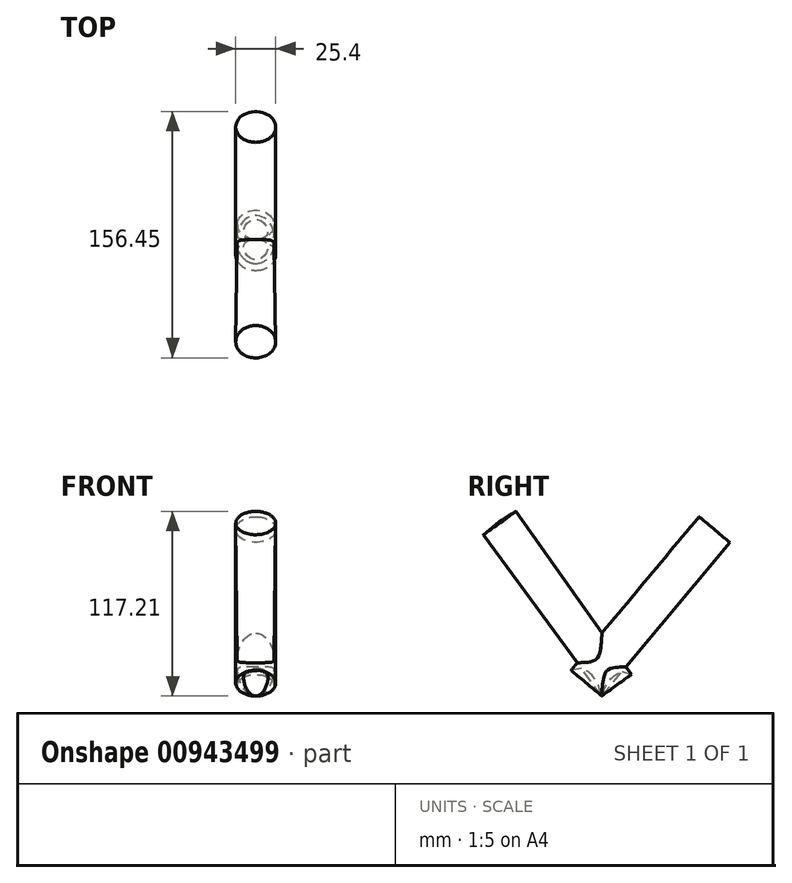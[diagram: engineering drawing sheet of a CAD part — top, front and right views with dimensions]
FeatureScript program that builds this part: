
annotation { "Feature Type Name" : "Feature", "Feature Type Description" : "" }
export const myFeature = defineFeature(function(context is Context, id is Id, definition is map)
    precondition{}
    {
        {
            var Q0;
            Q0=qCreatedBy(makeId("Right.planeOp"),FACE);
            var sketch = newSketch(context, id + "F0", { "sketchPlane" : qUnion([Q0])});
            skLineSegment(sketch, "E0", {"start": v(-105.27, 49.35) * mm, "end": v(-30.13, -53.04) * mm});
            skLineSegment(sketch, "E1", {"start": v(-30.13, -53.04) * mm, "end": v(51.18, 44.53) * mm});
            skLineSegment(sketch, "E2", {"start": v(51.18, 44.53) * mm, "end": v(41.42, 52.66) * mm});
            skLineSegment(sketch, "E3", {"start": v(41.42, 52.66) * mm, "end": v(-30.13, -33.2) * mm});
            skLineSegment(sketch, "E4", {"start": v(-30.13, -33.2) * mm, "end": v(-95.5, 57.45) * mm});
            skLineSegment(sketch, "E5", {"start": v(-95.5, 57.45) * mm, "end": v(-105.27, 49.35) * mm});
            skLineSegment(sketch, "E6", {"start": v(-30.13, -53.04) * mm, "end": v(-30.13, -33.2) * mm});
            skSolve(sketch);
        }
        {
            var Q0;
            Q0=makeQuery(id+"F0.imprint","IMPRINT",FACE,{"disambiguationData":[TD([[makeQuery(id+"F0.imprint","IMPRINT",EDGE,{"derivedFrom":sQuery(id+"F0.wireOp",EDGE,"E0")}),1.0]])]});
            var Q1;
            Q1=sQuery(id+"F0.wireOp",EDGE,"E4");
            revolve(context, id + "F1", {"surfaceOperationType" : NewSurfaceOperationType.NEW, "entities" : qUnion([Q0]), "axis" : qUnion([Q1]), "revolveType" : RevolveType.FULL});
        }
        {
            var Q0;
            Q0=makeQuery(id+"F0.imprint","IMPRINT",FACE,{"disambiguationData":[TD([[makeQuery(id+"F0.imprint","IMPRINT",EDGE,{"derivedFrom":sQuery(id+"F0.wireOp",EDGE,"E1")}),1.0]])]});
            var Q1;
            Q1=sQuery(id+"F0.wireOp",EDGE,"E3");
            revolve(context, id + "F2", {"operationType" : NewBodyOperationType.ADD, "surfaceOperationType" : NewSurfaceOperationType.NEW, "entities" : qUnion([Q0]), "axis" : qUnion([Q1]), "revolveType" : RevolveType.FULL});
        }
    });
